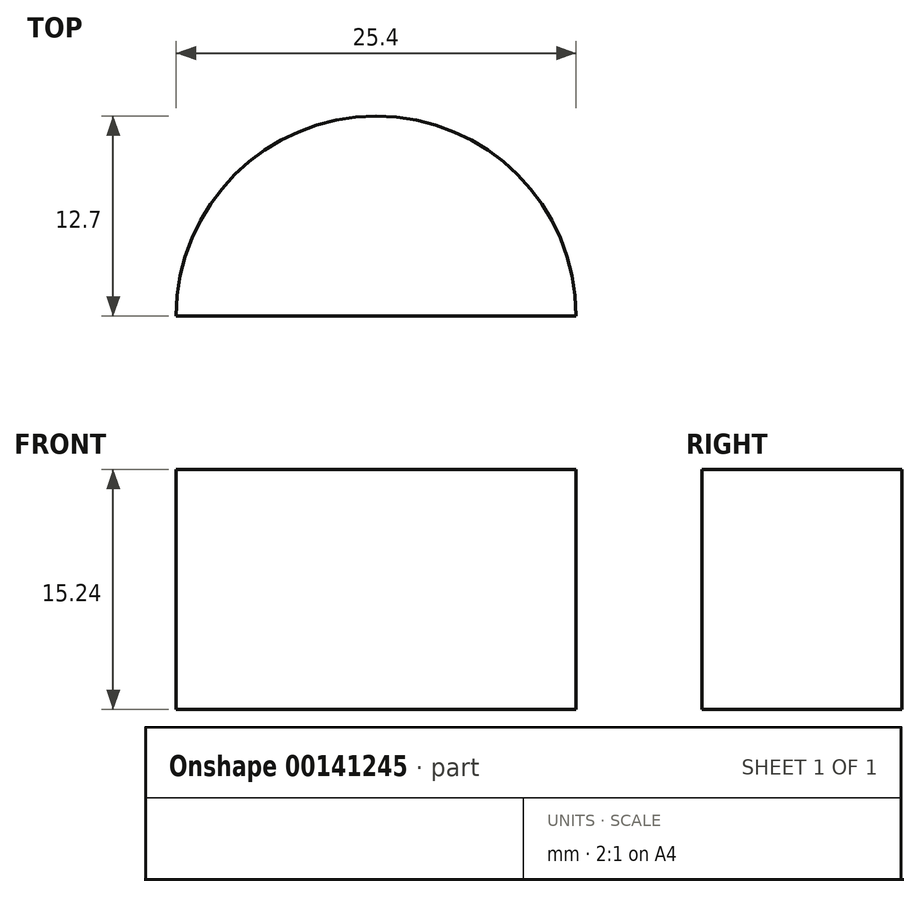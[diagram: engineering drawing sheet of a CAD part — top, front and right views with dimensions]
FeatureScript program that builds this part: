
annotation { "Feature Type Name" : "Feature", "Feature Type Description" : "" }
export const myFeature = defineFeature(function(context is Context, id is Id, definition is map)
    precondition{}
    {
        {
            var Q0;
            Q0=qCreatedBy(makeId("Top.planeOp"),FACE);
            var sketch = newSketch(context, id + "F0", { "sketchPlane" : qUnion([Q0])});
            skLineSegment(sketch, "E0", {"start": v(-15.41, -17.43) * mm, "end": v(9.99, -17.43) * mm});
            skArc(sketch, "E1", {"start": v(9.99, -17.43) * mm, "mid": v(-2.71, -4.73) * mm, "end": v(-15.41, -17.43) * mm});
            skSolve(sketch);
        }
        {
            var Q0;
            Q0=makeQuery(id+"F0.imprint","IMPRINT",FACE,{"disambiguationData":[TD([[makeQuery(id+"F0.imprint","IMPRINT",EDGE,{"derivedFrom":sQuery(id+"F0.wireOp",EDGE,"E0")}),1.0]])]});
            extrude(context, id + "F1", {"entities" : qUnion([Q0]), "depth" : 15.24 * mm});
        }
    });
